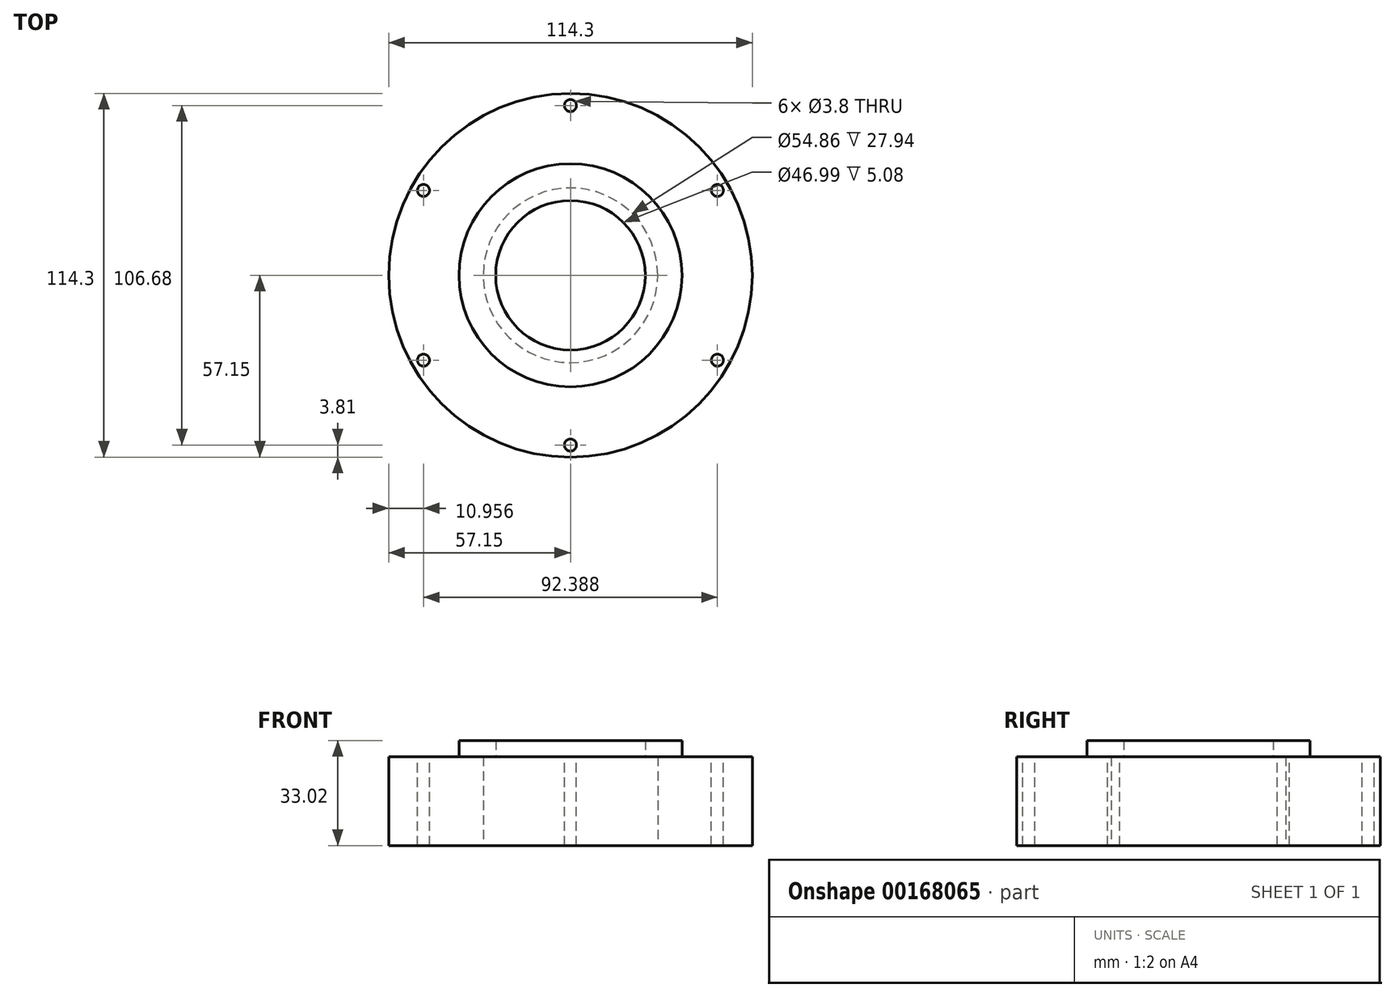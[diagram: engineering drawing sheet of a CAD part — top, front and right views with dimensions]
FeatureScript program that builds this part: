
annotation { "Feature Type Name" : "Feature", "Feature Type Description" : "" }
export const myFeature = defineFeature(function(context is Context, id is Id, definition is map)
    precondition{}
    {
        {
            var Q0;
            Q0=qCreatedBy(makeId("Top.planeOp"),FACE);
            var sketch = newSketch(context, id + "F0", { "sketchPlane" : qUnion([Q0])});
            skCircle(sketch, "E0", {"center": v(0, 0) * mm, "radius": 57.15 * mm});
            skCircle(sketch, "E1", {"center": v(0, 0) * mm, "radius": 27.43 * mm});
            skSolve(sketch);
        }
        {
            var Q0;
            Q0=qSketchRegion(id+"F0",true);
            extrude(context, id + "F1", {"entities" : qUnion([Q0]), "depth" : 27.94 * mm});
        }
        {
            var Q0;
            Q0=makeQuery(id+"F1.opExtrude","CAP_FACE",FACE,{"disambiguationData":[OSD([sQuery(id+"F0.wireOp",EDGE,"E0"),sQuery(id+"F0.wireOp",EDGE,"E1")])],"isStart":false});
            var sketch = newSketch(context, id + "F2", { "sketchPlane" : qUnion([Q0])});
            skCircle(sketch, "E2", {"center": v(0, 0) * mm, "radius": 35.05 * mm});
            skCircle(sketch, "E3", {"center": v(0, 0) * mm, "radius": 23.5 * mm});
            skSolve(sketch);
        }
        {
            var Q0;
            Q0=qSketchRegion(id+"F2",true);
            extrude(context, id + "F3", {"entities" : qUnion([Q0]), "operationType" : NewBodyOperationType.ADD, "depth" : 5.08 * mm});
        }
        {
            var Q0;
            Q0=makeQuery(id+"F1.opExtrude","CAP_FACE",FACE,{"disambiguationData":[OSD([sQuery(id+"F0.wireOp",EDGE,"E0"),sQuery(id+"F0.wireOp",EDGE,"E1")])],"isStart":false});
            var sketch = newSketch(context, id + "F4", { "sketchPlane" : qUnion([Q0])});
            skLineSegment(sketch, "E4", {"start": v(0, 0) * mm, "end": v(0, -53.34) * mm, "construction": true});
            skPoint(sketch, "E5", {"position": v(0, -53.34) * mm});
            skPoint(sketch, "E6.1.0", {"position": v(46.2, -26.67) * mm});
            skPoint(sketch, "E6.2.0", {"position": v(46.2, 26.67) * mm});
            skPoint(sketch, "E6.3.0", {"position": v(0, 53.34) * mm});
            skPoint(sketch, "E6.4.0", {"position": v(-46.2, 26.67) * mm});
            skPoint(sketch, "E6.5.0", {"position": v(-46.2, -26.67) * mm});
            skPoint(sketch, "E6.center", {"position": v(0, 0) * mm});
            skSolve(sketch);
        }
        {
            var Q0;
            Q0=sQuery(id+"F4.wireOp",VERTEX,"E5");
            var Q1;
            Q1=sQuery(id+"F4.wireOp",VERTEX,"E6.1.0");
            var Q2;
            Q2=sQuery(id+"F4.wireOp",VERTEX,"E6.2.0");
            var Q3;
            Q3=sQuery(id+"F4.wireOp",VERTEX,"E6.3.0");
            var Q4;
            Q4=sQuery(id+"F4.wireOp",VERTEX,"E6.4.0");
            var Q5;
            Q5=sQuery(id+"F4.wireOp",VERTEX,"E6.5.0");
            var Q6;
            Q6=makeQuery(id+"F1.opExtrude","SWEPT_BODY",BODY,{"disambiguationData":[OSD([sQuery(id+"F0.wireOp",EDGE,"E0"),sQuery(id+"F0.wireOp",EDGE,"E1")])]});
            hole(context, id + "F5", {"style" : HoleStyle.SIMPLE, "endStyle" : HoleEndStyle.THROUGH, "standardTappedOrClearance" : lookupTablePath({ "standard" : "ANSI", "fit" : "Normal (ASME)", "size" : "#6", "type" : "Clearance" }), "standardBlindInLast" : lookupTablePath({ "fit" : "Free", "standard" : "ANSI", "size" : "#6", "type" : "Clearance" }), "holeDiameter" : 3.8 * mm, "locations" : qUnion([Q0, Q1, Q2, Q3, Q4, Q5]), "scope" : qUnion([Q6]), "isTappedThrough" : true});
        }
    });
